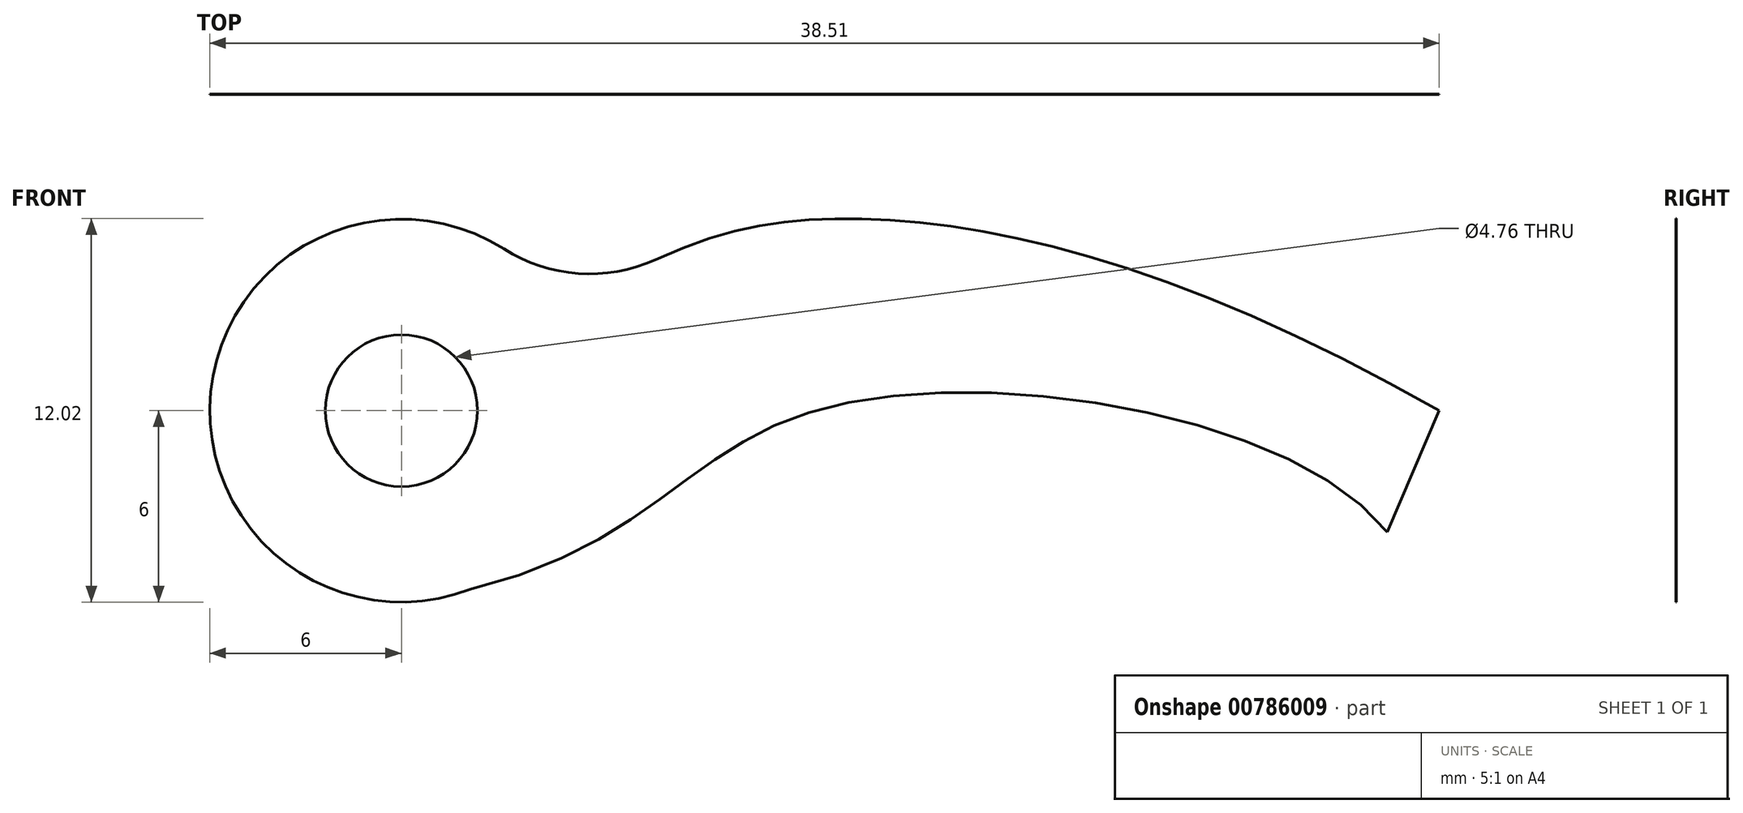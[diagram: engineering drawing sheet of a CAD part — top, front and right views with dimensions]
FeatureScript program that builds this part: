
annotation { "Feature Type Name" : "Feature", "Feature Type Description" : "" }
export const myFeature = defineFeature(function(context is Context, id is Id, definition is map)
    precondition{}
    {
        {
            var Q0;
            Q0=qCreatedBy(makeId("Front.planeOp"),FACE);
            var sketch = newSketch(context, id + "F0", { "sketchPlane" : qUnion([Q0])});
            skCircle(sketch, "E0", {"center": v(0, 0) * mm, "radius": 2.38 * mm});
            skCircle(sketch, "E1", {"center": v(0, 0) * mm, "radius": 6 * mm});
            skArc(sketch, "E2.0.startCap", {"start": v(5.03, -3.27) * mm, "mid": v(-3.27, -5.03) * mm, "end": v(-5.03, 3.27) * mm});
            skFitSpline(sketch, "E3", {"points": [v(0, 0) * mm, v(13.71, 6.02) * mm, v(32.5, 0) * mm], "startDerivative": vector(47.44, 31.61) * mm, "endDerivative": vector(46.76, -26.6) * mm});
            skLineSegment(sketch, "E4", {"start": v(32.5, 0) * mm, "end": v(30.88, -3.8) * mm});
            skFitSpline(sketch, "E5", {"points": [v(0, -6) * mm, v(12.96, 0) * mm, v(30.88, -3.8) * mm], "startDerivative": vector(48.6, 6.64) * mm, "endDerivative": vector(17.2, -21.5) * mm});
            skSolve(sketch);
        }
        {
            var Q0;
            Q0=qSketchRegion(id+"F0",true);
            extrude(context, id + "F1", {"entities" : qUnion([Q0]), "depth" : 1 / 203.2 * mm, "offsetDistance" : 25 * mm});
        }
        {
            var Q0;
            Q0=makeQuery(id+"F1.opExtrude","SWEPT_EDGE",EDGE,{"disambiguationData":[OSD([sQuery(id+"F0.wireOp",EDGE,"E1"),sQuery(id+"F0.wireOp",EDGE,"E3")])]});
            fillet(context, id + "F2", {"entities" : qUnion([Q0]), "radius" : 5 * mm, "tangentPropagation" : true, "allowEdgeOverflow" : false});
        }
    });
